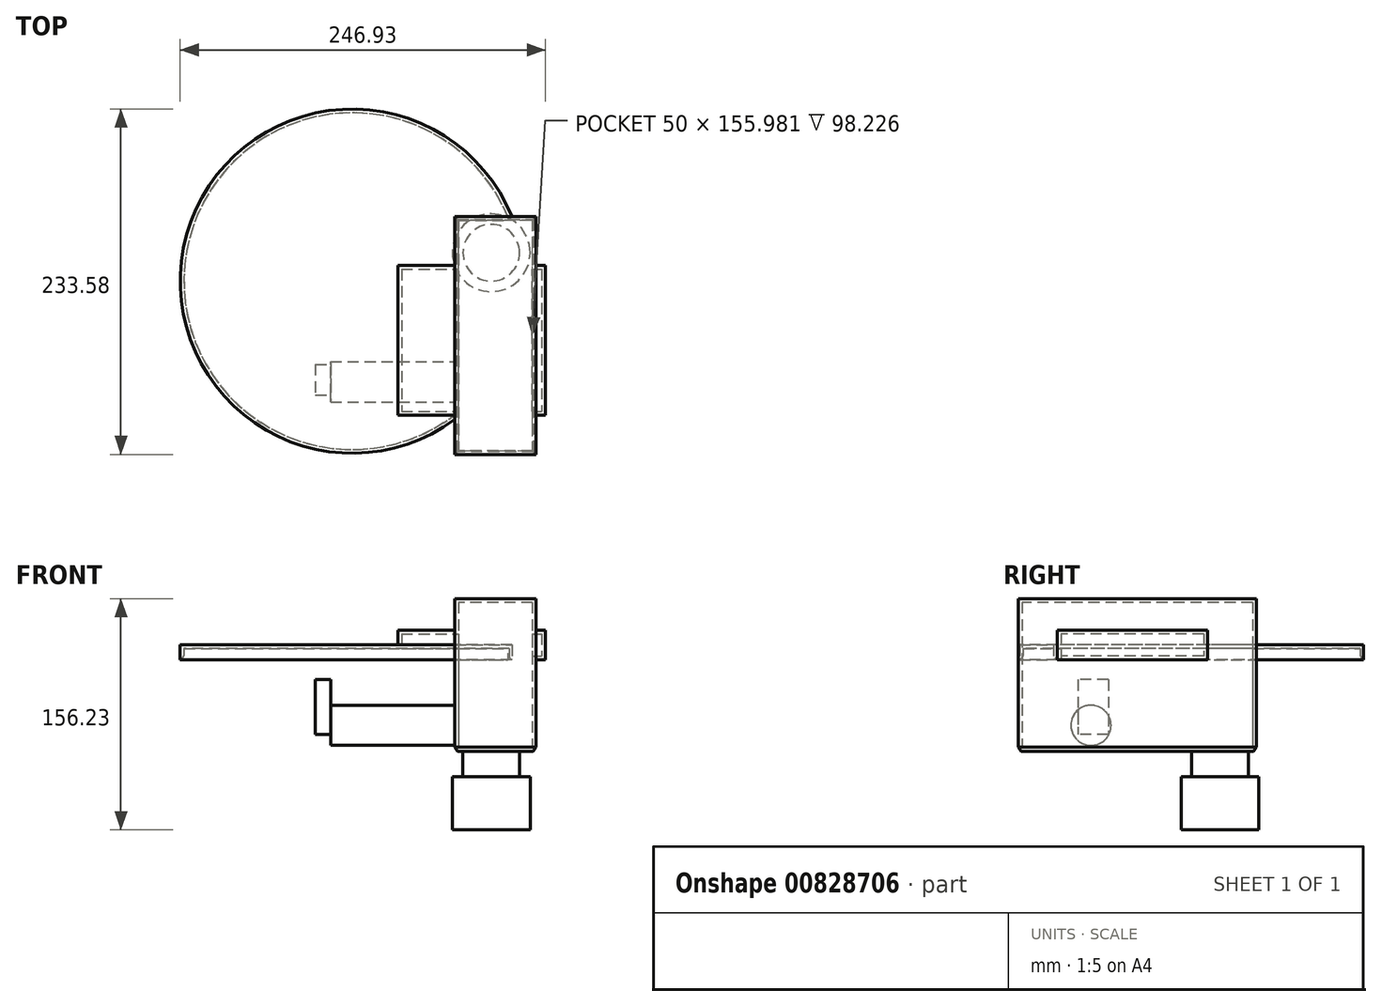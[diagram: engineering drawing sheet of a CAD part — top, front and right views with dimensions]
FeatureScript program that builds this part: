
annotation { "Feature Type Name" : "Feature", "Feature Type Description" : "" }
export const myFeature = defineFeature(function(context is Context, id is Id, definition is map)
    precondition{}
    {
        {
            var Q0;
            Q0=qCreatedBy(makeId("Top.planeOp"),FACE);
            var sketch = newSketch(context, id + "F0", { "sketchPlane" : qUnion([Q0])});
            skLineSegment(sketch, "E0.bottom", {"start": v(-38.48, 49.44) * mm, "end": v(61.31, 49.44) * mm});
            skLineSegment(sketch, "E0.top", {"start": v(-38.48, -51.92) * mm, "end": v(61.31, -51.92) * mm});
            skLineSegment(sketch, "E0.left", {"start": v(-38.48, 49.44) * mm, "end": v(-38.48, -51.92) * mm});
            skLineSegment(sketch, "E0.right", {"start": v(61.31, 49.44) * mm, "end": v(61.31, -51.92) * mm});
            skSolve(sketch);
        }
        {
            var Q0;
            Q0=makeQuery(id+"F0.imprint","IMPRINT",FACE,{"disambiguationData":[TD([[makeQuery(id+"F0.imprint","IMPRINT",EDGE,{"derivedFrom":sQuery(id+"F0.wireOp",EDGE,"E0.bottom")}),-1.0]])]});
            extrude(context, id + "F1", {"entities" : qUnion([Q0]), "depth" : 20 * mm, "offsetDistance" : 25 * mm});
        }
        {
            var Q0;
            Q0=qCreatedBy(makeId("Right.planeOp"),FACE);
            var sketch = newSketch(context, id + "F2", { "sketchPlane" : qUnion([Q0])});
            skLineSegment(sketch, "E1.bottom", {"start": v(82.56, 41.24) * mm, "end": v(-78.42, 41.24) * mm});
            skLineSegment(sketch, "E1.top", {"start": v(82.56, -61.99) * mm, "end": v(-78.42, -61.99) * mm});
            skLineSegment(sketch, "E1.left", {"start": v(82.56, 41.24) * mm, "end": v(82.56, -61.99) * mm});
            skLineSegment(sketch, "E1.right", {"start": v(-78.42, 41.24) * mm, "end": v(-78.42, -61.99) * mm});
            skSolve(sketch);
        }
        {
            var Q0;
            Q0 = qSketchRegion(id + "F2", true);
            extrude(context, id + "F3", {"entities" : qUnion([Q0]), "operationType" : NewBodyOperationType.ADD, "depth" : 55 * mm, "offsetDistance" : 25 * mm});
        }
        {
            var Q0;
            Q0=qCreatedBy(makeId("Top.planeOp"),FACE);
            var sketch = newSketch(context, id + "F4", { "sketchPlane" : qUnion([Q0])});
            skCircle(sketch, "E2", {"center": v(-69.27, 38.8) * mm, "radius": 116.35 * mm});
            skSolve(sketch);
        }
        {
            var Q0;
            Q0=makeQuery(id+"F4.imprint","IMPRINT",FACE,{"disambiguationData":[TD([[makeQuery(id+"F4.imprint","IMPRINT",EDGE,{"derivedFrom":sQuery(id+"F4.wireOp",EDGE,"E2")}),1.0]])]});
            extrude(context, id + "F5", {"entities" : qUnion([Q0]), "operationType" : NewBodyOperationType.ADD, "depth" : 10 * mm, "offsetDistance" : 25 * mm});
        }
        {
            var Q0;
            {var subQ0=sQuery(id+"F0.wireOp",EDGE,"E0.bottom");var subQ1=sQuery(id+"F0.wireOp",EDGE,"E0.top");var subQ2=sQuery(id+"F0.wireOp",EDGE,"E0.left");Q0=makeQuery(id+"F5.boolean.opBoolean","MERGE",FACE,{"derivedFrom":[makeQuery(id+"F3.boolean.opBoolean","SPLIT",FACE,{"disambiguationData":[TD([makeQuery(id+"F1.opExtrude","SWEPT_FACE",FACE,{"disambiguationData":[OSD([subQ2])]})])],"derivedFrom":makeQuery(id+"F1.opExtrude","CAP_FACE",FACE,{"disambiguationData":[OSD([subQ0,subQ1,subQ2,sQuery(id+"F0.wireOp",EDGE,"E0.right")])],"isStart":true})}),makeQuery(id+"F5.opExtrude","CAP_FACE",FACE,{"disambiguationData":[OSD([sQuery(id+"F4.wireOp",EDGE,"E2")])],"isStart":true})]});}
            shell(context, id + "F6", {"entities" : qUnion([Q0]), "thickness" : 2.5 * mm});
        }
        {
            var Q0;
            Q0=makeQuery(id+"F3.opExtrude","CAP_FACE",FACE,{"disambiguationData":[OSD([sQuery(id+"F2.wireOp",EDGE,"E1.bottom"),sQuery(id+"F2.wireOp",EDGE,"E1.top"),sQuery(id+"F2.wireOp",EDGE,"E1.left"),sQuery(id+"F2.wireOp",EDGE,"E1.right")])],"isStart":true});
            var sketch = newSketch(context, id + "F7", { "sketchPlane" : qUnion([Q0])});
            skCircle(sketch, "E3", {"center": v(29.22, -44.39) * mm, "radius": 13.57 * mm});
            skSolve(sketch);
        }
        {
            var Q0;
            Q0 = qSketchRegion(id + "F7", true);
            extrude(context, id + "F8", {"entities" : qUnion([Q0]), "operationType" : NewBodyOperationType.ADD, "depth" : 84 * mm, "offsetDistance" : 25 * mm});
        }
        {
            var Q0;
            Q0=makeQuery(id+"F8.opExtrude","CAP_FACE",FACE,{"disambiguationData":[OSD([sQuery(id+"F7.wireOp",EDGE,"E3")])],"isStart":false});
            var sketch = newSketch(context, id + "F9", { "sketchPlane" : qUnion([Q0])});
            skLineSegment(sketch, "E4.bottom", {"start": v(37.87, -51.18) * mm, "end": v(17.8, -51.18) * mm});
            skLineSegment(sketch, "E4.top", {"start": v(37.87, -13.98) * mm, "end": v(17.8, -13.98) * mm});
            skLineSegment(sketch, "E4.left", {"start": v(37.87, -51.18) * mm, "end": v(37.87, -13.98) * mm});
            skLineSegment(sketch, "E4.right", {"start": v(17.8, -51.18) * mm, "end": v(17.8, -13.98) * mm});
            skSolve(sketch);
        }
        {
            var Q0;
            Q0=makeQuery(id+"F3.opExtrude","SWEPT_FACE",FACE,{"disambiguationData":[OSD([sQuery(id+"F2.wireOp",EDGE,"E1.top")])]});
            chamfer(context, id + "F10", {"entities" : qUnion([Q0]), "chamferType" : ChamferType.TWO_OFFSETS, "width1" : 3 * mm, "oppositeDirection" : false, "width2" : 2 * mm, "tangentPropagation" : true});
        }
        {
            var Q0;
            {var subQ0=sQuery(id+"F9.wireOp",EDGE,"E4.bottom");Q0=makeQuery(id+"F9.imprint","IMPRINT",FACE,{"disambiguationData":[TD([[makeQuery(id+"F9.imprint","IMPRINT",EDGE,{"derivedFrom":subQ0}),-1.0]])]});}
            var sketch = newSketch(context, id + "F11", { "sketchPlane" : qUnion([Q0])});
            skLineSegment(sketch, "E5.bottom", {"start": v(17.48, -13.52) * mm, "end": v(38.08, -13.52) * mm});
            skLineSegment(sketch, "E5.top", {"start": v(17.48, -50.65) * mm, "end": v(38.08, -50.65) * mm});
            skLineSegment(sketch, "E5.left", {"start": v(17.48, -13.52) * mm, "end": v(17.48, -50.65) * mm});
            skLineSegment(sketch, "E5.right", {"start": v(38.08, -13.52) * mm, "end": v(38.08, -50.65) * mm});
            skSolve(sketch);
        }
        {
            var Q0;
            Q0 = qSketchRegion(id + "F11", true);
            extrude(context, id + "F12", {"entities" : qUnion([Q0]), "operationType" : NewBodyOperationType.ADD, "depth" : 10.3 * mm, "offsetDistance" : 25 * mm});
        }
        {
            var Q0;
            {var subQ0=sQuery(id+"F4.wireOp",EDGE,"E2");Q0=makeQuery(id+"F6.opShell","OFFSET_EDGE",EDGE,{"disambiguationData":[OSD([subQ0]),TDD([makeQuery(id+"F5.opExtrude","CAP_EDGE",EDGE,{"disambiguationData":[OSD([subQ0])],"isStart":true})]),OD(2.0)]});}
            fillet(context, id + "F13", {"entities" : qUnion([Q0]), "radius" : 5 * mm, "tangentPropagation" : true, "allowEdgeOverflow" : false});
        }
        {
            var Q0;
            Q0=makeQuery(id+"F3.opExtrude","SWEPT_FACE",FACE,{"disambiguationData":[OSD([sQuery(id+"F2.wireOp",EDGE,"E1.top")])]});
            var sketch = newSketch(context, id + "F14", { "sketchPlane" : qUnion([Q0])});
            skCircle(sketch, "E6", {"center": v(24.63, -58.04) * mm, "radius": 19.17 * mm});
            skSolve(sketch);
        }
        {
            var Q0;
            Q0=makeQuery(id+"F14.imprint","IMPRINT",FACE,{"disambiguationData":[TD([[makeQuery(id+"F14.imprint","IMPRINT",EDGE,{"derivedFrom":sQuery(id+"F14.wireOp",EDGE,"E6")}),1.0]])]});
            extrude(context, id + "F15", {"entities" : qUnion([Q0]), "operationType" : NewBodyOperationType.ADD, "depth" : 53 * mm, "offsetDistance" : 25 * mm});
        }
        {
            var Q0;
            Q0=makeQuery(id+"F15.opExtrude","CAP_FACE",FACE,{"disambiguationData":[OSD([sQuery(id+"F14.wireOp",EDGE,"E6")])],"isStart":false});
            var sketch = newSketch(context, id + "F16", { "sketchPlane" : qUnion([Q0])});
            skCircle(sketch, "E7", {"center": v(24.63, -58.04) * mm, "radius": 26.3 * mm});
            skSolve(sketch);
        }
        {
            var Q0;
            Q0=makeQuery(id+"F16.imprint","IMPRINT",FACE,{"disambiguationData":[TD([[makeQuery(id+"F16.imprint","IMPRINT",EDGE,{"derivedFrom":sQuery(id+"F16.wireOp",EDGE,"E7")}),1.0]])]});
            var Q1;
            Q1=makeQuery(id+"F16.imprint","IMPRINT",FACE,{"disambiguationData":[TD([[makeQuery(id+"F16.imprint","IMPRINT",EDGE,{"derivedFrom":makeQuery(id+"F15.opExtrude","CAP_EDGE",EDGE,{"disambiguationData":[OSD([sQuery(id+"F14.wireOp",EDGE,"E6")])],"isStart":false})}),1.0]])]});
            extrude(context, id + "F17", {"entities" : qUnion([Q0, Q1]), "operationType" : NewBodyOperationType.ADD, "oppositeDirection" : true, "depth" : 36 * mm, "offsetDistance" : 25 * mm});
        }
    });
